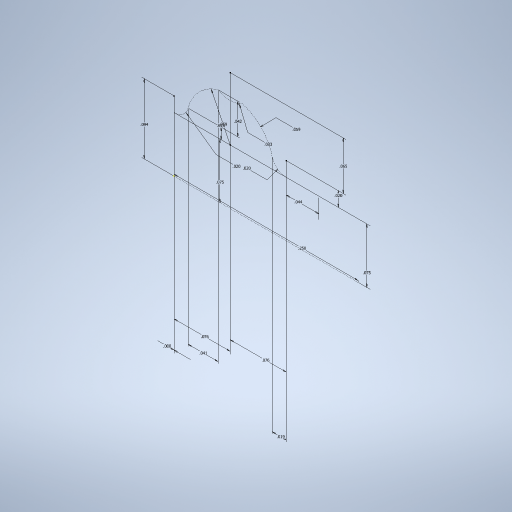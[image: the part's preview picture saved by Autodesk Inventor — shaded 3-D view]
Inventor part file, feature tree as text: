
AUTODESK INVENTOR PART (.ipt)
format: ipt  version: 2023.3 (Build 273359000, 359)  size: 249,856 bytes
history: native  units: in
note: dims shown in document units (in); Inventor stores cm internally (conversion verified against a paired STEP export)
features: sketch x1
ambient origin geometry x8: Origin, YZ Plane, XZ Plane, XY Plane, X Axis, Y Axis, Z Axis, Center Point
feature tree (1):
  sketch  "Sketch1"  dims[d1=0.0444in d2=0.0197in d3=0.0591in d4=0.0328in d5=0.0591in d6=0.0197in d7=0.0748in d8=0.0945in d9=0.0762in d10=0.0762in d11=0.0655in d12=0.0197in d13=0.0748in d14=0.0in d15=0.25in d16=0.0191in d17=0.0408in d18=0.0148in d19=0.042in]
